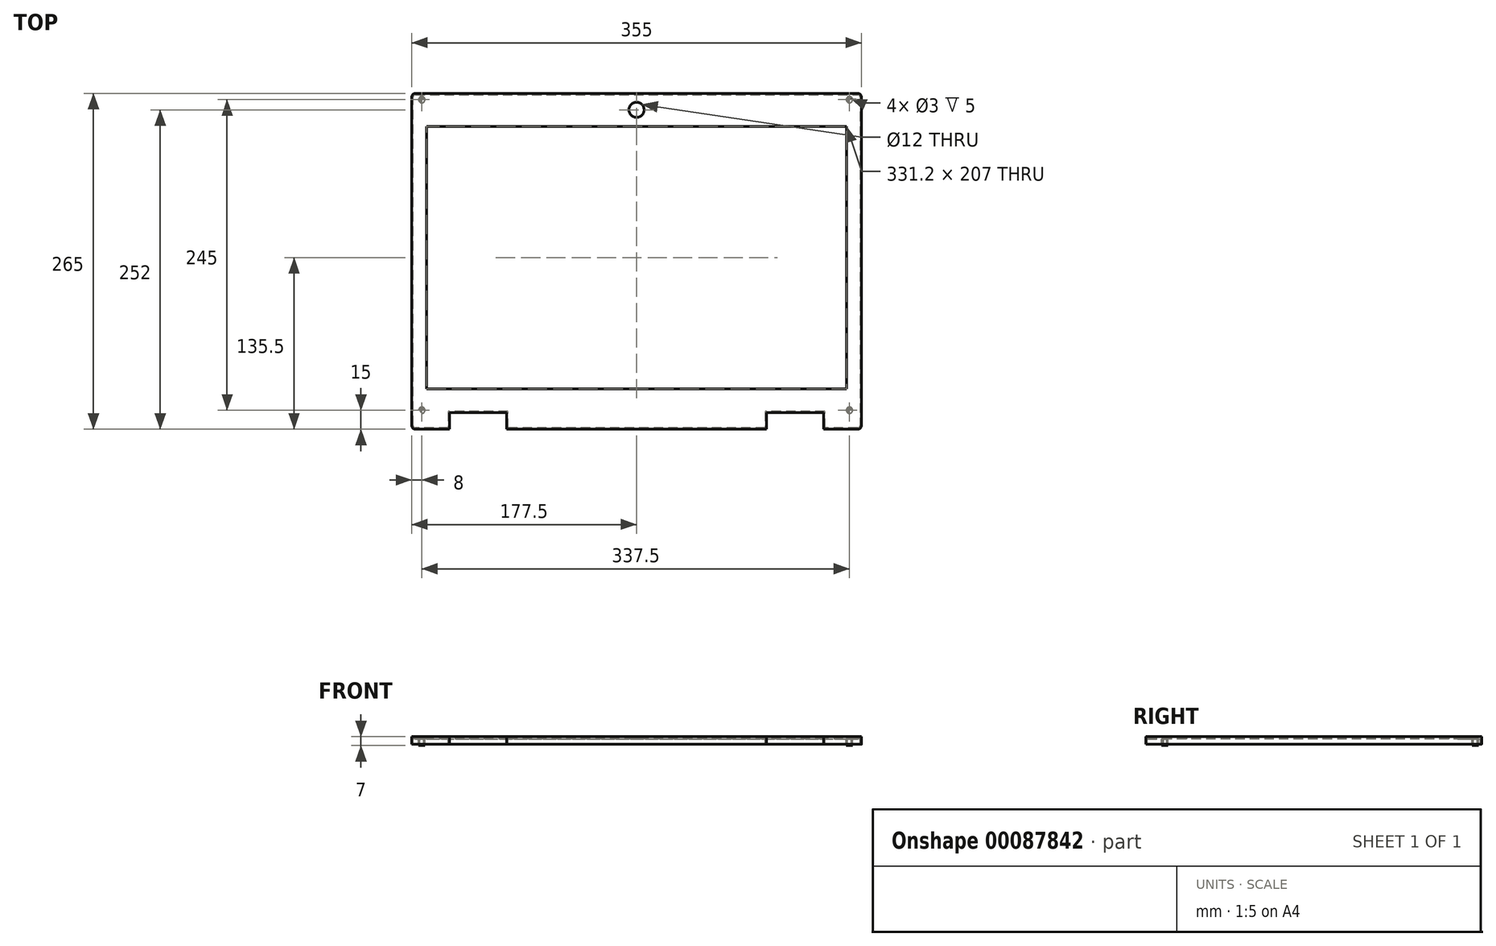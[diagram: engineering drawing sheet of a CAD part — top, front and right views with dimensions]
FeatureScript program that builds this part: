
annotation { "Feature Type Name" : "Feature", "Feature Type Description" : "" }
export const myFeature = defineFeature(function(context is Context, id is Id, definition is map)
    precondition{}
    {
        {
            var Q0;
            Q0=qCreatedBy(makeId("Top.planeOp"),FACE);
            var sketch = newSketch(context, id + "F0", { "sketchPlane" : qUnion([Q0])});
            skLineSegment(sketch, "E0.top", {"start": v(174.5, 132.5) * mm, "end": v(-174.5, 132.5) * mm});
            skLineSegment(sketch, "E0.left", {"start": v(177.5, -129.5) * mm, "end": v(177.5, 129.5) * mm});
            skLineSegment(sketch, "E0.right", {"start": v(-177.5, -129.5) * mm, "end": v(-177.5, 129.5) * mm});
            skPoint(sketch, "E0.middle", {"position": v(0, 0) * mm});
            skPoint(sketch, "E1.visualSharp", {"position": v(-177.5, 132.5) * mm});
            skArc(sketch, "E1.filletArc", {"start": v(-174.5, 132.5) * mm, "mid": v(-176.62, 131.62) * mm, "end": v(-177.5, 129.5) * mm});
            skPoint(sketch, "E2.visualSharp", {"position": v(177.5, 132.5) * mm});
            skArc(sketch, "E2.filletArc", {"start": v(177.5, 129.5) * mm, "mid": v(176.62, 131.62) * mm, "end": v(174.5, 132.5) * mm});
            skPoint(sketch, "E3.visualSharp", {"position": v(177.5, -132.5) * mm});
            skArc(sketch, "E3.filletArc", {"start": v(174.5, -132.5) * mm, "mid": v(176.62, -131.62) * mm, "end": v(177.5, -129.5) * mm});
            skPoint(sketch, "E4.visualSharp", {"position": v(-177.5, -132.5) * mm});
            skArc(sketch, "E4.filletArc", {"start": v(-177.5, -129.5) * mm, "mid": v(-176.62, -131.62) * mm, "end": v(-174.5, -132.5) * mm});
            skLineSegment(sketch, "E5.bottom", {"start": v(-165.6, 106.5) * mm, "end": v(165.6, 106.5) * mm});
            skLineSegment(sketch, "E5.top", {"start": v(-165.6, -100.5) * mm, "end": v(165.6, -100.5) * mm});
            skLineSegment(sketch, "E5.left", {"start": v(-165.6, 106.5) * mm, "end": v(-165.6, -100.5) * mm});
            skLineSegment(sketch, "E5.right", {"start": v(165.6, 106.5) * mm, "end": v(165.6, -100.5) * mm});
            skCircle(sketch, "E6", {"center": v(0, 119.5) * mm, "radius": 6 * mm});
            skLineSegment(sketch, "E7.top", {"start": v(102.5, -119.5) * mm, "end": v(147.5, -119.5) * mm});
            skLineSegment(sketch, "E7.left", {"start": v(102.5, -132.5) * mm, "end": v(102.5, -119.5) * mm});
            skLineSegment(sketch, "E7.right", {"start": v(147.5, -132.5) * mm, "end": v(147.5, -119.5) * mm});
            skLineSegment(sketch, "E8.top", {"start": v(-102.5, -119.5) * mm, "end": v(-147.5, -119.5) * mm});
            skLineSegment(sketch, "E8.left", {"start": v(-102.5, -132.5) * mm, "end": v(-102.5, -119.5) * mm});
            skLineSegment(sketch, "E8.right", {"start": v(-147.5, -132.5) * mm, "end": v(-147.5, -119.5) * mm});
            skLineSegment(sketch, "E9", {"start": v(147.5, -132.5) * mm, "end": v(174.5, -132.5) * mm});
            skLineSegment(sketch, "E10", {"start": v(102.5, -132.5) * mm, "end": v(-102.5, -132.5) * mm});
            skLineSegment(sketch, "E11", {"start": v(-147.5, -132.5) * mm, "end": v(-174.5, -132.5) * mm});
            skSolve(sketch);
        }
        {
            var Q0;
            Q0=makeQuery(id+"F0.imprint","IMPRINT",FACE,{"disambiguationData":[TD([[makeQuery(id+"F0.imprint","IMPRINT",EDGE,{"derivedFrom":sQuery(id+"F0.wireOp",EDGE,"E0.top")}),1.0]])]});
            extrude(context, id + "F1", {"entities" : qUnion([Q0]), "depth" : 2 * mm});
        }
        {
            var Q0;
            Q0=makeQuery(id+"F1.opExtrude","CAP_FACE",FACE,{"disambiguationData":[OSD([sQuery(id+"F0.wireOp",EDGE,"E0.bottom"),sQuery(id+"F0.wireOp",EDGE,"E0.top"),sQuery(id+"F0.wireOp",EDGE,"E0.left"),sQuery(id+"F0.wireOp",EDGE,"E0.right"),sQuery(id+"F0.wireOp",EDGE,"E1.filletArc"),sQuery(id+"F0.wireOp",EDGE,"E2.filletArc"),sQuery(id+"F0.wireOp",EDGE,"E3.filletArc"),sQuery(id+"F0.wireOp",EDGE,"E4.filletArc"),sQuery(id+"F0.wireOp",EDGE,"E5.bottom"),sQuery(id+"F0.wireOp",EDGE,"E5.top"),sQuery(id+"F0.wireOp",EDGE,"E5.left"),sQuery(id+"F0.wireOp",EDGE,"E5.right"),sQuery(id+"F0.wireOp",EDGE,"E6"),sQuery(id+"F0.wireOp",EDGE,"E7.top"),sQuery(id+"F0.wireOp",EDGE,"E7.left"),sQuery(id+"F0.wireOp",EDGE,"E7.right"),sQuery(id+"F0.wireOp",EDGE,"E8.top"),sQuery(id+"F0.wireOp",EDGE,"E8.left"),sQuery(id+"F0.wireOp",EDGE,"E8.right")])],"isStart":true});
            var sketch = newSketch(context, id + "F2", { "sketchPlane" : qUnion([Q0])});
            skCircle(sketch, "E12", {"center": v(-169.5, 117.5) * mm, "radius": 2.5 * mm});
            skCircle(sketch, "E13", {"center": v(-169.5, 117.5) * mm, "radius": 1.5 * mm});
            skCircle(sketch, "E14", {"center": v(168, 117.5) * mm, "radius": 2.5 * mm});
            skCircle(sketch, "E15", {"center": v(168, 117.5) * mm, "radius": 1.5 * mm});
            skCircle(sketch, "E16", {"center": v(-169.5, -127.5) * mm, "radius": 2.5 * mm});
            skCircle(sketch, "E17", {"center": v(-169.5, -127.5) * mm, "radius": 1.5 * mm});
            skCircle(sketch, "E18", {"center": v(168, -127.5) * mm, "radius": 2.5 * mm});
            skCircle(sketch, "E19", {"center": v(168, -127.5) * mm, "radius": 1.5 * mm});
            skSolve(sketch);
        }
        {
            var Q0;
            Q0=qSketchRegion(id+"F2",true);
            extrude(context, id + "F3", {"entities" : qUnion([Q0]), "operationType" : NewBodyOperationType.ADD, "depth" : 5 * mm});
        }
        {
            var Q0;
            {var subQ0=sQuery(id+"F0.wireOp",EDGE,"E11");var subQ1=sQuery(id+"F0.wireOp",EDGE,"E7.top");var subQ2=sQuery(id+"F0.wireOp",EDGE,"E7.left");var subQ3=sQuery(id+"F0.wireOp",EDGE,"E10");var subQ4=sQuery(id+"F0.wireOp",EDGE,"E9");var subQ5=sQuery(id+"F0.wireOp",EDGE,"E5.right");var subQ6=sQuery(id+"F0.wireOp",EDGE,"E8.right");var subQ7=sQuery(id+"F0.wireOp",EDGE,"E8.top");var subQ8=sQuery(id+"F0.wireOp",EDGE,"E6");var subQ9=sQuery(id+"F0.wireOp",EDGE,"E1.filletArc");var subQ10=sQuery(id+"F0.wireOp",EDGE,"E0.right");var subQ11=sQuery(id+"F0.wireOp",EDGE,"E0.left");var subQ12=sQuery(id+"F0.wireOp",EDGE,"E5.top");var subQ13=sQuery(id+"F0.wireOp",EDGE,"E8.left");var subQ14=sQuery(id+"F0.wireOp",EDGE,"E0.top");var subQ15=sQuery(id+"F0.wireOp",EDGE,"E2.filletArc");var subQ16=sQuery(id+"F0.wireOp",EDGE,"E3.filletArc");var subQ17=sQuery(id+"F0.wireOp",EDGE,"E4.filletArc");var subQ18=sQuery(id+"F0.wireOp",EDGE,"E7.right");var subQ19=sQuery(id+"F0.wireOp",EDGE,"E5.bottom");var subQ20=sQuery(id+"F0.wireOp",EDGE,"E5.left");Q0=makeQuery(id+"F3.boolean.opBoolean","SPLIT",FACE,{"disambiguationData":[TD([makeQuery(id+"F1.opExtrude","SWEPT_FACE",FACE,{"disambiguationData":[OSD([subQ14])]})])],"derivedFrom":makeQuery(id+"F1.opExtrude","CAP_FACE",FACE,{"disambiguationData":[OSD([subQ14,subQ11,subQ10,subQ9,subQ15,subQ16,subQ17,subQ19,subQ12,subQ20,subQ5,subQ8,subQ1,subQ2,subQ18,subQ7,subQ13,subQ6,subQ4,subQ3,subQ0])],"isStart":true})});}
            var sketch = newSketch(context, id + "F4", { "sketchPlane" : qUnion([Q0])});
            skLineSegment(sketch, "E20", {"start": v(-174.5, -132.5) * mm, "end": v(174.5, -132.5) * mm});
            skLineSegment(sketch, "E21", {"start": v(177.5, -129.5) * mm, "end": v(177.5, 129.5) * mm});
            skLineSegment(sketch, "E22", {"start": v(174.5, 132.5) * mm, "end": v(147.5, 132.5) * mm});
            skLineSegment(sketch, "E23", {"start": v(147.5, 132.5) * mm, "end": v(147.5, 119.5) * mm});
            skLineSegment(sketch, "E24", {"start": v(147.5, 119.5) * mm, "end": v(102.5, 119.5) * mm});
            skLineSegment(sketch, "E25", {"start": v(102.5, 119.5) * mm, "end": v(102.5, 132.5) * mm});
            skLineSegment(sketch, "E26", {"start": v(102.5, 132.5) * mm, "end": v(-102.5, 132.5) * mm});
            skLineSegment(sketch, "E27", {"start": v(-102.5, 132.5) * mm, "end": v(-102.5, 119.5) * mm});
            skLineSegment(sketch, "E28", {"start": v(-102.5, 119.5) * mm, "end": v(-147.5, 119.5) * mm});
            skLineSegment(sketch, "E29", {"start": v(-147.5, 119.5) * mm, "end": v(-147.5, 132.5) * mm});
            skLineSegment(sketch, "E30", {"start": v(-147.5, 132.5) * mm, "end": v(-174.5, 132.5) * mm});
            skLineSegment(sketch, "E31", {"start": v(-177.5, 129.5) * mm, "end": v(-177.5, -129.5) * mm});
            skPoint(sketch, "E32.visualSharp", {"position": v(-177.5, -132.5) * mm});
            skArc(sketch, "E32.filletArc", {"start": v(-177.5, -129.5) * mm, "mid": v(-176.62, -131.62) * mm, "end": v(-174.5, -132.5) * mm});
            skPoint(sketch, "E33.visualSharp", {"position": v(177.5, -132.5) * mm});
            skArc(sketch, "E33.filletArc", {"start": v(174.5, -132.5) * mm, "mid": v(176.62, -131.62) * mm, "end": v(177.5, -129.5) * mm});
            skPoint(sketch, "E34.visualSharp", {"position": v(177.5, 132.5) * mm});
            skArc(sketch, "E34.filletArc", {"start": v(177.5, 129.5) * mm, "mid": v(176.62, 131.62) * mm, "end": v(174.5, 132.5) * mm});
            skPoint(sketch, "E35.visualSharp", {"position": v(-177.5, 132.5) * mm});
            skArc(sketch, "E35.filletArc", {"start": v(-174.5, 132.5) * mm, "mid": v(-176.62, 131.62) * mm, "end": v(-177.5, 129.5) * mm});
            skArc(sketch, "E36.0", {"start": v(-176.5, -129.5) * mm, "mid": v(-175.91, -130.91) * mm, "end": v(-174.5, -131.5) * mm});
            skLineSegment(sketch, "E36.1", {"start": v(-176.5, 129.5) * mm, "end": v(-176.5, -129.5) * mm});
            skArc(sketch, "E36.2", {"start": v(-174.5, 131.5) * mm, "mid": v(-175.91, 130.91) * mm, "end": v(-176.5, 129.5) * mm});
            skLineSegment(sketch, "E36.3", {"start": v(-148.5, 131.5) * mm, "end": v(-174.5, 131.5) * mm});
            skLineSegment(sketch, "E36.4", {"start": v(-148.5, 118.5) * mm, "end": v(-148.5, 131.5) * mm});
            skLineSegment(sketch, "E36.5", {"start": v(174.5, 131.5) * mm, "end": v(148.5, 131.5) * mm});
            skArc(sketch, "E36.6", {"start": v(176.5, 129.5) * mm, "mid": v(175.91, 130.91) * mm, "end": v(174.5, 131.5) * mm});
            skLineSegment(sketch, "E36.7", {"start": v(176.5, -129.5) * mm, "end": v(176.5, 129.5) * mm});
            skArc(sketch, "E36.8", {"start": v(174.5, -131.5) * mm, "mid": v(175.91, -130.91) * mm, "end": v(176.5, -129.5) * mm});
            skLineSegment(sketch, "E36.9", {"start": v(148.5, 131.5) * mm, "end": v(148.5, 118.5) * mm});
            skLineSegment(sketch, "E36.10", {"start": v(148.5, 118.5) * mm, "end": v(101.5, 118.5) * mm});
            skLineSegment(sketch, "E36.11", {"start": v(101.5, 118.5) * mm, "end": v(101.5, 131.5) * mm});
            skLineSegment(sketch, "E36.12", {"start": v(101.5, 131.5) * mm, "end": v(-101.5, 131.5) * mm});
            skLineSegment(sketch, "E36.13", {"start": v(-101.5, 131.5) * mm, "end": v(-101.5, 118.5) * mm});
            skLineSegment(sketch, "E36.14", {"start": v(-174.5, -131.5) * mm, "end": v(174.5, -131.5) * mm});
            skLineSegment(sketch, "E36.15", {"start": v(-101.5, 118.5) * mm, "end": v(-148.5, 118.5) * mm});
            skSolve(sketch);
        }
        {
            var Q0;
            Q0 = qSketchRegion(id + "F4", true);
            extrude(context, id + "F5", {"entities" : qUnion([Q0]), "operationType" : NewBodyOperationType.ADD, "depth" : 4 * mm});
        }
    });
